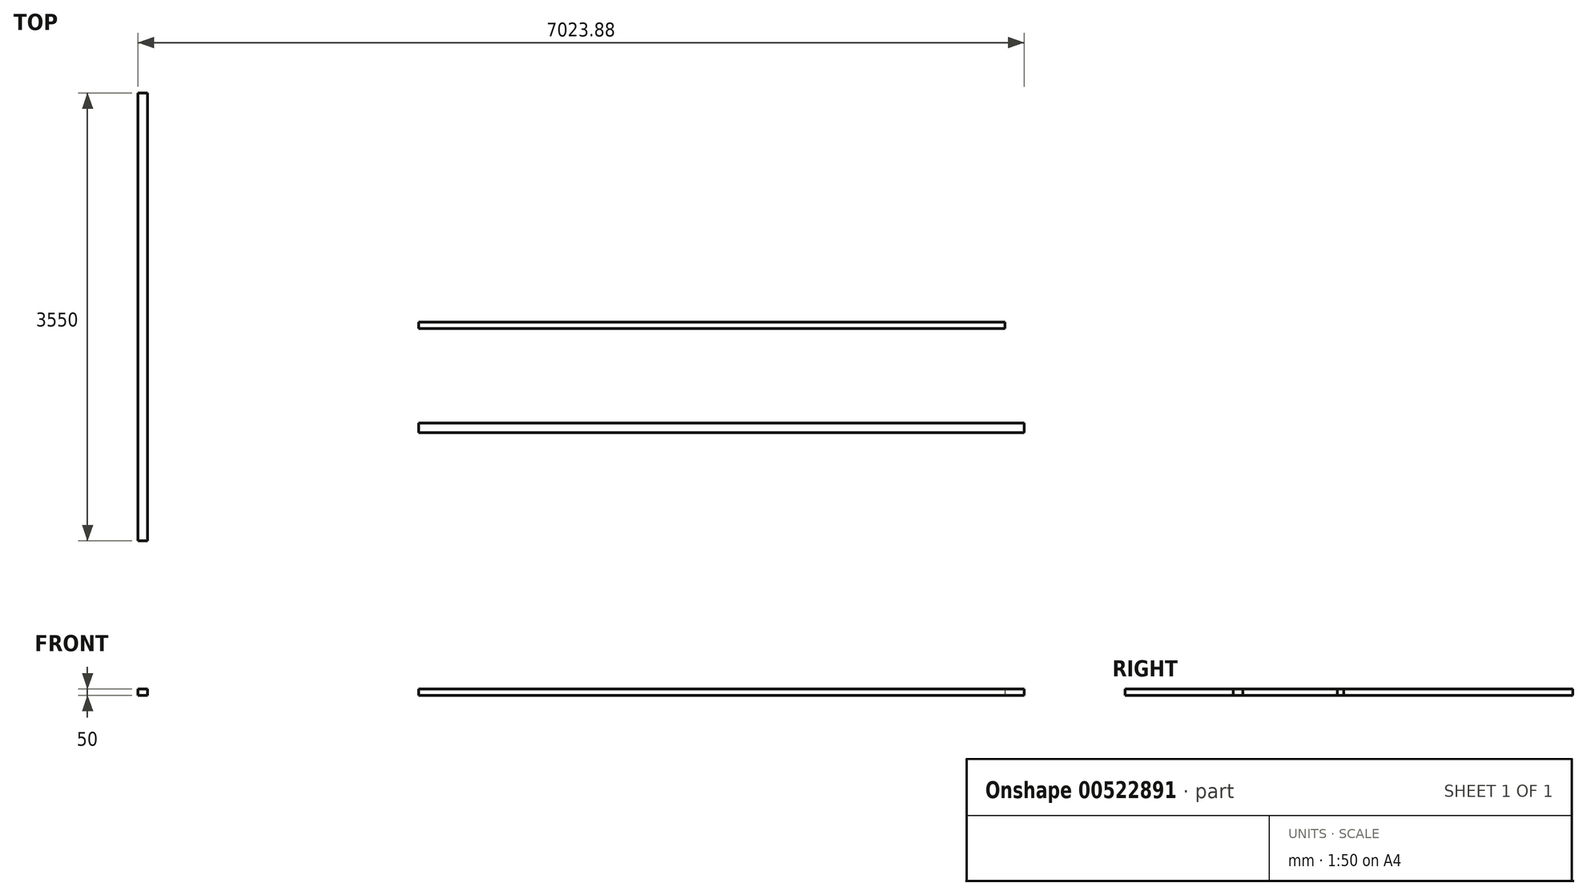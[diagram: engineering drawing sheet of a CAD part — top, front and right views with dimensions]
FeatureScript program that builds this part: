
annotation { "Feature Type Name" : "Feature", "Feature Type Description" : "" }
export const myFeature = defineFeature(function(context is Context, id is Id, definition is map)
    precondition{}
    {
        {
            var Q0;
            Q0=qCreatedBy(makeId("Top.planeOp"),FACE);
            var sketch = newSketch(context, id + "F0", { "sketchPlane" : qUnion([Q0])});
            skLineSegment(sketch, "E0", {"start": v(-883.42, -80.45) * mm, "end": v(3916.58, -80.45) * mm});
            skLineSegment(sketch, "E1", {"start": v(3916.58, -80.45) * mm, "end": v(3916.58, -5.45) * mm});
            skLineSegment(sketch, "E2", {"start": v(3916.58, -5.45) * mm, "end": v(-883.42, -5.45) * mm});
            skLineSegment(sketch, "E3", {"start": v(-883.42, -5.45) * mm, "end": v(-883.42, -80.45) * mm});
            skLineSegment(sketch, "E4", {"start": v(-3107.3, -938.7) * mm, "end": v(-3107.3, 2611.3) * mm});
            skLineSegment(sketch, "E5", {"start": v(-3032.3, 2611.3) * mm, "end": v(-3032.3, -938.7) * mm});
            skLineSegment(sketch, "E6", {"start": v(-3032.3, -938.7) * mm, "end": v(-3107.3, -938.7) * mm});
            skLineSegment(sketch, "E7", {"start": v(-3107.3, 2611.3) * mm, "end": v(-3032.3, 2611.3) * mm});
            skLineSegment(sketch, "E8", {"start": v(-883.42, 745.77) * mm, "end": v(3766.58, 745.77) * mm});
            skLineSegment(sketch, "E9", {"start": v(3766.58, 745.77) * mm, "end": v(3766.58, 795.77) * mm});
            skLineSegment(sketch, "E10", {"start": v(3766.58, 795.77) * mm, "end": v(-883.42, 795.77) * mm});
            skLineSegment(sketch, "E11", {"start": v(-883.42, 795.77) * mm, "end": v(-883.42, 745.77) * mm});
            skPoint(sketch, "E12", {"position": v(-3057.3, 2036.3) * mm});
            skPoint(sketch, "E13", {"position": v(-3057.3, 1436.3) * mm});
            skPoint(sketch, "E14", {"position": v(-3057.3, 836.3) * mm});
            skPoint(sketch, "E15", {"position": v(-3057.3, 236.3) * mm});
            skPoint(sketch, "E16", {"position": v(-3057.3, -363.7) * mm});
            skSolve(sketch);
        }
        {
            var Q0;
            Q0=makeQuery(id+"F0.imprint","IMPRINT",FACE,{"disambiguationData":[TD([[makeQuery(id+"F0.imprint","IMPRINT",EDGE,{"derivedFrom":sQuery(id+"F0.wireOp",EDGE,"E0")}),1.0]])]});
            var Q1;
            Q1=makeQuery(id+"F0.imprint","IMPRINT",FACE,{"disambiguationData":[TD([[makeQuery(id+"F0.imprint","IMPRINT",EDGE,{"derivedFrom":sQuery(id+"F0.wireOp",EDGE,"E8")}),1.0]])]});
            var Q2;
            Q2=makeQuery(id+"F0.imprint","IMPRINT",FACE,{"disambiguationData":[TD([[makeQuery(id+"F0.imprint","IMPRINT",EDGE,{"derivedFrom":sQuery(id+"F0.wireOp",EDGE,"E4")}),-1.0]])]});
            extrude(context, id + "F1", {"entities" : qUnion([Q0, Q1, Q2]), "depth" : 50 * mm, "offsetDistance" : 25 * mm});
        }
    });
